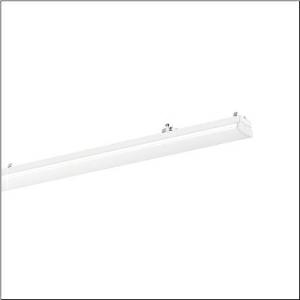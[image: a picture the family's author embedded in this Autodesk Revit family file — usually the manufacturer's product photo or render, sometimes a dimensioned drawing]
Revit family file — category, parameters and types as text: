
# Revit family: licross_r__11_recessed_opal_ho_51te1dmn4d5m_4002
name_source: partatom
category: Lighting Fixtures
units: mm (PartAtom-declared; Revit-internal decimal feet)

## family parameters
Cut with Voids When Loaded = No
Host = Face
Light Source = No
Part Type = Normal
Room Calculation Point = No
Round Connector Dimension = Use Diameter
Shared = No

## types (1)
- --- (1 x LED, 13690 lm, 74.5 W, 4000K)
    Apparent Load = 75 VA
    CIE Flux Codes = 44 73 91 87 100
    Color Rendering = 80
    Color Temperature = 4000K
    Default Elevation = 1800 mm
    Description = Licross® 11 recessed opal HO, luminaire insert, of sheet steel, coil coated, white, length: 1.500mm, width: 76mm, height: 87mm, LED rated luminous flux: 13.690lm, light colour: 840, control gear: ON/OFF Multilumen, with plug, 3-pole, with phase selection, mains connection: 220..240V, AC, 50/60Hz, rated input power: 75W, internal wiring halogen-free, primary optical cover: cover, of PMMA, light emission: direct with ceiling illumination distribution, primary light characteristic: symmetric, protection rating (complete): IP54, insulation class (complete): insulation class I (protective earthing), certification: CE, ENEC, VDE, UKCA, protection symbol: D if used in an environment with non-conductive dust loads with corresponding accessories, impact resistance: IK06, permissible ambient temperature for indoor applications: -35..+35°C, corresponds to IFS (International Featured Standards) requirements for safety and quality in the food industry, reducing of maximum allowable ambient temperature of 5°C with ceiling mounting, packaging unit: 1 piece
    Height = 83 mm
    Lamp = 1 x LED
    Lamp Light Flux = 13690 lm
    Lamp Power = 74.5 W
    Lamp count = 1
    Length = 1500 mm
    Luminous efficacy = 184 lm/W
    Manufacturer = Siteco
    ModVariant = No
    Model = 51TE1DMN4D5M
    Mounting Place = Ceiling
    Mounting Type = Pendant
    Number of Poles = 1
    OnlyDefault = Yes
    Power Factor = 1
    Product Name = Licross® 11 recessed opal HO
    Product group = luminaire insert | ceiling pendant
    ProductGroupID = 902
    Protection Class = Protection class I
    Protection Degree = IP 54
    RLX_Detail_Level = 1
    RLX_Emergency_Light_Flux = 0 lm
    RLX_Emergency_Type = 0
    RLX_Emergency_Type_DB = No
    RlxData = <blob elided: 24805 chars, md5=6a16b3b1>
    Socket = socket
    Standby Power = 0 W
    System Light Flux = 13690 lm
    System Power = 75 W
    Type Comments = factory setting: luminous flux: 100 % | (A | C | E) | 174 mA
    Type Image = l_1313666.jpg
    URL = http://relux.com
    VarID = @adj_097295
    Voltage = 0 V
    Weight = 0.00 kg
    Width = 76 mm

## geometry (parser evidence)
native form markers: Blend x4, Sweep x13
no freeform markers — native parametric forms only
